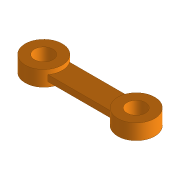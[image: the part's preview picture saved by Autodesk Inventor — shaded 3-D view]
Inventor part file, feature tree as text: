
AUTODESK INVENTOR PART (.ipt)
format: ipt  version: 2017 (Build 210142000, 142)  size: 104,960 bytes
history: native  units: mm
features: extrude x2, sketch x2, mirror x1
ambient origin geometry x8: Origin, YZ Plane, XZ Plane, XY Plane, X Axis, Y Axis, Z Axis, Center Point
bodies: Solid1 (feature_tree)
feature tree (5):
  extrude  "Extrusion1"  Depth=6.0mm
  extrude  "Extrusion2"  Depth=7.0mm
  mirror  "Mirror1"
  sketch  "Sketch1"  dims[d0=30.0mm d1=6.0mm]
  sketch  "Sketch2"  dims[d2=12.0mm d3=7.0mm d4=5.0mm d5=0.0mm d6=1.5mm d7=0.0mm]
